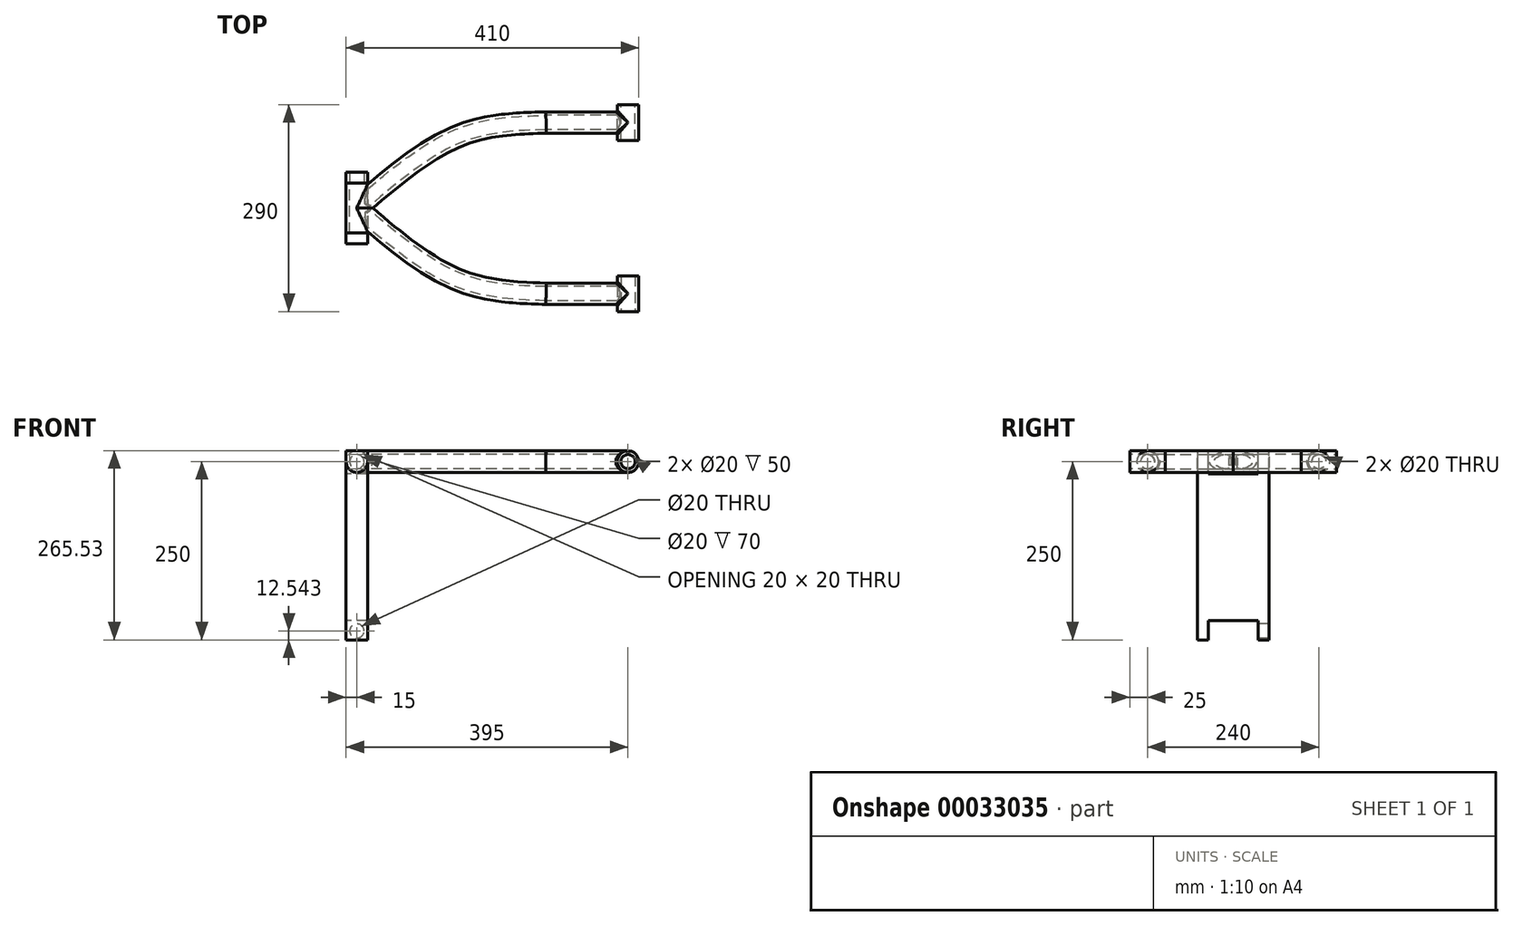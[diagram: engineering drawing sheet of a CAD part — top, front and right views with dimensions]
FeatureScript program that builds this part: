
annotation { "Feature Type Name" : "Feature", "Feature Type Description" : "" }
export const myFeature = defineFeature(function(context is Context, id is Id, definition is map)
    precondition{}
    {
        {
            var Q0;
            Q0=qCreatedBy(makeId("Front.planeOp"),FACE);
            var sketch = newSketch(context, id + "F0", { "sketchPlane" : qUnion([Q0])});
            skCircle(sketch, "E0", {"center": v(0, 0) * mm, "radius": 15 * mm});
            skCircle(sketch, "E1", {"center": v(0, 0) * mm, "radius": 10 * mm});
            skLineSegment(sketch, "E2", {"start": v(-15, 31.18) * mm, "end": v(-15, -34.32) * mm, "construction": true});
            skSolve(sketch);
        }
        {
            var Q0;
            Q0=makeQuery(id+"F0.imprint","IMPRINT",FACE,{"disambiguationData":[TD([[makeQuery(id+"F0.imprint","IMPRINT",EDGE,{"derivedFrom":sQuery(id+"F0.wireOp",EDGE,"E0")}),1.0]])]});
            extrude(context, id + "F1", {"entities" : qUnion([Q0]), "depth" : 50 * mm});
        }
        {
            var Q0;
            Q0=qCreatedBy(makeId("Right.planeOp"),FACE);
            var sketch = newSketch(context, id + "F2", { "sketchPlane" : qUnion([Q0])});
            skLineSegment(sketch, "E3", {"start": v(0, -15) * mm, "end": v(-50, -15) * mm});
            skLineSegment(sketch, "E4", {"start": v(-50, 15) * mm, "end": v(0, 15) * mm});
            skCircle(sketch, "E5", {"center": v(-25, 0) * mm, "radius": 15 * mm});
            skPoint(sketch, "E5.centerSnap0", {"position": v(-25, 15) * mm});
            skCircle(sketch, "E6", {"center": v(-25, 0) * mm, "radius": 10 * mm});
            skSolve(sketch);
        }
        {
            var Q0;
            Q0=qCreatedBy(makeId("Top.planeOp"),FACE);
            var sketch = newSketch(context, id + "F3", { "sketchPlane" : qUnion([Q0])});
            skLineSegment(sketch, "E7", {"start": v(0, -37.06) * mm, "end": v(0, -397.44) * mm, "construction": true});
            skLineSegment(sketch, "E8", {"start": v(-380, 0) * mm, "end": v(-380, -571.82) * mm, "construction": true});
            skLineSegment(sketch, "E9", {"start": v(76.72, -145) * mm, "end": v(-436.32, -145) * mm, "construction": true});
            skLineSegment(sketch, "E10", {"start": v(0, -25.32) * mm, "end": v(-114.87, -25.32) * mm});
            skFitSpline(sketch, "E11", {"points": [v(-114.87, -25.32) * mm, v(-237.42, -44.08) * mm, v(-380, -145) * mm], "startDerivative": vector(-269.22, -7.9) * mm, "endDerivative": vector(-261.26, -225.26) * mm});
            skLineSegment(sketch, "E12.MirrorCS", {"start": v(0, -264.68) * mm, "end": v(-114.87, -264.68) * mm});
            skFitSpline(sketch, "E13.MirrorCS", {"points": [v(-114.87, -264.68) * mm, v(-237.42, -245.92) * mm, v(-380, -145) * mm], "startDerivative": vector(-269.22, 7.9) * mm, "endDerivative": vector(-261.26, 225.26) * mm});
            skSolve(sketch);
        }
        {
            var Q0;
            Q0 = qSketchRegion(id + "F2", true);
            var Q1;
            Q1=sQuery(id+"F3.wireOp",EDGE,"E11");
            var Q2;
            Q2=sQuery(id+"F3.wireOp",EDGE,"E10");
            sweep(context, id + "F4", {"operationType" : NewBodyOperationType.ADD, "profiles" : qUnion([Q0]), "path" : qUnion([Q1, Q2])});
        }
        {
            var Q0;
            Q0=makeQuery(id+"F4.boolean.opBoolean","INTERSECT",EDGE,{"disambiguationData":[OD(0.0)],"derivedFrom":[makeQuery(id+"F1.opExtrude","SWEPT_FACE",FACE,{"disambiguationData":[OSD([sQuery(id+"F0.wireOp",EDGE,"E0")])]}),makeQuery(id+"F4.opSweep","SWEPT_FACE",FACE,{"disambiguationData":[OSD([sQuery(id+"F2.wireOp",EDGE,"E5"),sQuery(id+"F3.wireOp",EDGE,"ba36500d-ebc8-4f5f-b360-66259673c2d1")])]})]});
            var Q1;
            Q1=makeQuery(id+"F4.boolean.opBoolean","INTERSECT",EDGE,{"disambiguationData":[OD(1.0)],"derivedFrom":[makeQuery(id+"F1.opExtrude","SWEPT_FACE",FACE,{"disambiguationData":[OSD([sQuery(id+"F0.wireOp",EDGE,"E0")])]}),makeQuery(id+"F4.opSweep","SWEPT_FACE",FACE,{"disambiguationData":[OSD([sQuery(id+"F2.wireOp",EDGE,"E5"),sQuery(id+"F3.wireOp",EDGE,"ba36500d-ebc8-4f5f-b360-66259673c2d1")])]})]});
            fillet(context, id + "F5", {"entities" : qUnion([Q0, Q1]), "radius" : 2 * mm, "tangentPropagation" : true, "allowEdgeOverflow" : false});
        }
        {
            var Q0;
            Q0=makeQuery(id+"F1.opExtrude","CAP_FACE",FACE,{"disambiguationData":[OSD([sQuery(id+"F0.wireOp",EDGE,"E0"),sQuery(id+"F0.wireOp",EDGE,"E1")])],"isStart":false});
            var sketch = newSketch(context, id + "F6", { "sketchPlane" : qUnion([Q0])});
            skCircle(sketch, "E14", {"center": v(0, 0) * mm, "radius": 10 * mm});
            skSolve(sketch);
        }
        {
            var Q0;
            Q0 = qSketchRegion(id + "F6", true);
            var Q1;
            Q1=makeQuery(id+"F6.imprint","IMPRINT",FACE,{"disambiguationData":[TD([[makeQuery(id+"F6.imprint","IMPRINT",EDGE,{"derivedFrom":sQuery(id+"F6.wireOp",EDGE,"E14")}),1.0]])]});
            extrude(context, id + "F7", {"entities" : qUnion([Q0, Q1]), "operationType" : NewBodyOperationType.REMOVE, "endBound" : BoundingType.THROUGH_ALL, "oppositeDirection" : true, "depth" : 25 * mm});
        }
        {
            var Q0;
            Q0=qCreatedBy(makeId("Front.planeOp"),FACE);
            cPlane(context, id + "F8", {"entities" : qUnion([Q0]), "cplaneType" : CPlaneType.OFFSET, "offset" : 145 * mm, "width" : 150 * mm, "height" : 150 * mm});
        }
        {
            var Q0;
            Q0=makeQuery(id+"F1.opExtrude","SWEPT_BODY",BODY,{"disambiguationData":[OSD([sQuery(id+"F0.wireOp",EDGE,"E0"),sQuery(id+"F0.wireOp",EDGE,"E1")])]});
            var Q1;
            Q1=qCreatedBy(id+"F8.planeOp",FACE);
            mirror(context, id + "F9", {"operationType" : NewBodyOperationType.ADD, "entities" : qUnion([Q0]), "mirrorPlane" : qUnion([Q1])});
        }
        {
            var Q0;
            Q0=qCreatedBy(id+"F8.planeOp",FACE);
            var sketch = newSketch(context, id + "F10", { "sketchPlane" : qUnion([Q0])});
            skLineSegment(sketch, "E15", {"start": v(0, 0) * mm, "end": v(-405.9, 0) * mm, "construction": true});
            skCircle(sketch, "E16", {"center": v(-380, 0) * mm, "radius": 15 * mm});
            skCircle(sketch, "E17", {"center": v(-380, 0) * mm, "radius": 10 * mm});
            skPoint(sketch, "E18.0", {"position": v(-380, 15) * mm});
            skLineSegment(sketch, "E19", {"start": v(-380, 15) * mm, "end": v(-380, -15) * mm, "construction": true});
            skSolve(sketch);
        }
        {
            var Q0;
            Q0 = qSketchRegion(id + "F10", true);
            extrude(context, id + "F11", {"entities" : qUnion([Q0]), "operationType" : NewBodyOperationType.ADD, "depth" : 70 * mm, "symmetric" : true});
        }
        {
            var Q0;
            Q0=makeQuery(id+"F11.opExtrude","CAP_FACE",FACE,{"disambiguationData":[OSD([sQuery(id+"F10.wireOp",EDGE,"E16"),sQuery(id+"F10.wireOp",EDGE,"E17")])],"isStart":false});
            var sketch = newSketch(context, id + "F12", { "sketchPlane" : qUnion([Q0])});
            skCircle(sketch, "E20", {"center": v(-380, 0) * mm, "radius": 10 * mm});
            skPoint(sketch, "E20.first.point", {"position": v(-378.85, 9.93) * mm});
            skPoint(sketch, "E20.second.point", {"position": v(-373.45, -7.56) * mm});
            skPoint(sketch, "E20.third.point", {"position": v(-388.96, -4.45) * mm});
            skSolve(sketch);
        }
        {
            var Q0;
            Q0=makeQuery(id+"F12.imprint","IMPRINT",FACE,{"disambiguationData":[TD([[makeQuery(id+"F12.imprint","IMPRINT",EDGE,{"derivedFrom":sQuery(id+"F12.wireOp",EDGE,"E20")}),1.0]])]});
            extrude(context, id + "F13", {"entities" : qUnion([Q0]), "operationType" : NewBodyOperationType.REMOVE, "endBound" : BoundingType.THROUGH_ALL, "oppositeDirection" : true, "depth" : 25 * mm});
        }
        {
            var Q0;
            Q0=makeQuery(id+"F11.opExtrude","CAP_FACE",FACE,{"disambiguationData":[OSD([sQuery(id+"F10.wireOp",EDGE,"E16"),sQuery(id+"F10.wireOp",EDGE,"E17")])],"isStart":false});
            var sketch = newSketch(context, id + "F14", { "sketchPlane" : qUnion([Q0])});
            skCircle(sketch, "E21", {"center": v(-380, 0) * mm, "radius": 10 * mm});
            skSolve(sketch);
        }
        {
            var Q0;
            Q0=makeQuery(id+"F14.imprint","IMPRINT",FACE,{"disambiguationData":[TD([[makeQuery(id+"F14.imprint","IMPRINT",EDGE,{"derivedFrom":sQuery(id+"F14.wireOp",EDGE,"E21")}),1.0]])]});
            extrude(context, id + "F15", {"entities" : qUnion([Q0]), "depth" : 100 * mm});
        }
        {
            var Q0;
            Q0=makeQuery(id+"F15.opExtrude","SWEPT_BODY",BODY,{"disambiguationData":[OSD([sQuery(id+"F14.wireOp",EDGE,"E21")])]});
            var Q1;
            {var subQ0=sQuery(id+"F10.wireOp",EDGE,"E16");var subQ1=sQuery(id+"F10.wireOp",EDGE,"E17");Q1=makeQuery(id+"F11.boolean.opBoolean","SPLIT",FACE,{"disambiguationData":[TD([makeQuery(id+"F11.opExtrude","CAP_FACE",FACE,{"disambiguationData":[OSD([subQ0,subQ1])],"isStart":true})])],"derivedFrom":makeQuery(id+"F11.opExtrude","SWEPT_FACE",FACE,{"disambiguationData":[OSD([subQ0])]})});}
            transform(context, id + "F16", {"entities" : qUnion([Q0]), "transformType" : TransformType.TRANSLATION_DISTANCE, "transformDirection" : qUnion([Q1]), "distance" : 85 * mm, "makeCopy" : false});
        }
        {
            var Q0;
            Q0=makeQuery(id+"F15.opExtrude","SWEPT_FACE",FACE,{"disambiguationData":[OSD([sQuery(id+"F14.wireOp",EDGE,"E21")])]});
            cPlane(context, id + "F17", {"entities" : qUnion([Q0]), "cplaneType" : CPlaneType.LINE_ANGLE, "offset" : 150 * mm, "angle" : 90 * degree, "width" : 150 * mm, "height" : 150 * mm});
        }
        {
            var Q0;
            Q0=qCreatedBy(id+"F17.planeOp",FACE);
            var sketch = newSketch(context, id + "F18", { "sketchPlane" : qUnion([Q0])});
            skLineSegment(sketch, "E22", {"start": v(-95, 10) * mm, "end": v(-95, -10) * mm});
            skLineSegment(sketch, "E23", {"start": v(-109.96, -16.97) * mm, "end": v(-180.1, -16.97) * mm});
            skLineSegment(sketch, "E24", {"start": v(-180.1, -16.97) * mm, "end": v(-180.1, -10) * mm});
            skLineSegment(sketch, "E25", {"start": v(-195, -10) * mm, "end": v(-195, 10) * mm});
            skLineSegment(sketch, "E26", {"start": v(-95, 0) * mm, "end": v(-195, 0) * mm, "construction": true});
            skLineSegment(sketch, "E27", {"start": v(-95, -10) * mm, "end": v(-95, -120) * mm});
            skLineSegment(sketch, "E28", {"start": v(-195, -120) * mm, "end": v(-195, -10) * mm});
            skLineSegment(sketch, "E29", {"start": v(-84.47, -120) * mm, "end": v(-204.44, -120) * mm, "construction": true});
            skLineSegment(sketch, "E30", {"start": v(-180.1, -10) * mm, "end": v(-180.1, 10) * mm});
            skLineSegment(sketch, "E31", {"start": v(-95, -120) * mm, "end": v(-195, -120) * mm});
            skLineSegment(sketch, "E32.MirrorCS", {"start": v(-95, -230) * mm, "end": v(-95, -120) * mm});
            skLineSegment(sketch, "E33.MirrorCS", {"start": v(-95, -250) * mm, "end": v(-95, -230) * mm});
            skLineSegment(sketch, "E34.MirrorCS", {"start": v(-109.96, -223.03) * mm, "end": v(-180.1, -223.03) * mm});
            skLineSegment(sketch, "E35.MirrorCS", {"start": v(-195, -230) * mm, "end": v(-195, -250) * mm});
            skLineSegment(sketch, "E36.MirrorCS", {"start": v(-195, -120) * mm, "end": v(-195, -230) * mm});
            skLineSegment(sketch, "E37", {"start": v(-95, -250) * mm, "end": v(-109.96, -250) * mm});
            skLineSegment(sketch, "E38", {"start": v(-109.96, -250) * mm, "end": v(-109.96, -223.03) * mm});
            skLineSegment(sketch, "E39", {"start": v(-180.1, -250) * mm, "end": v(-195, -250) * mm});
            skLineSegment(sketch, "E40", {"start": v(-109.96, -16.97) * mm, "end": v(-109.96, 10) * mm});
            skLineSegment(sketch, "E41", {"start": v(-95, 10) * mm, "end": v(-95, 15.53) * mm});
            skLineSegment(sketch, "E42", {"start": v(-95, 15.53) * mm, "end": v(-109.96, 15.53) * mm});
            skLineSegment(sketch, "E43", {"start": v(-180.1, 10) * mm, "end": v(-180.1, 15.47) * mm});
            skLineSegment(sketch, "E44", {"start": v(-180.1, 15.47) * mm, "end": v(-195, 15.47) * mm});
            skLineSegment(sketch, "E45", {"start": v(-195, 15.47) * mm, "end": v(-195, 10) * mm});
            skLineSegment(sketch, "E46", {"start": v(-109.96, 10) * mm, "end": v(-109.96, 15.53) * mm});
            skLineSegment(sketch, "E47", {"start": v(-180.1, -250) * mm, "end": v(-180.1, -223.03) * mm});
            skSolve(sketch);
        }
        {
            var Q0;
            Q0=makeQuery(id+"F18.imprint","IMPRINT",FACE,{"disambiguationData":[TD([[makeQuery(id+"F18.imprint","IMPRINT",EDGE,{"derivedFrom":sQuery(id+"F18.wireOp",EDGE,"E31")}),1.0]])]});
            var Q1;
            {var subQ2=sQuery(id+"F18.wireOp",EDGE,"E22");Q1=makeQuery(id+"F18.imprint","IMPRINT",FACE,{"disambiguationData":[TD([[makeQuery(id+"F18.imprint","IMPRINT",EDGE,{"derivedFrom":subQ2}),-1.0]])]});}
            extrude(context, id + "F19", {"entities" : qUnion([Q0, Q1]), "operationType" : NewBodyOperationType.ADD, "depth" : 30 * mm, "symmetric" : true});
        }
        {
            var Q0;
            Q0=makeQuery(id+"F19.opExtrude","SWEPT_FACE",FACE,{"disambiguationData":[OSD([sQuery(id+"F18.wireOp",EDGE,"E38")])]});
            var sketch = newSketch(context, id + "F20", { "sketchPlane" : qUnion([Q0])});
            skCircle(sketch, "E48", {"center": v(-380, -237.46) * mm, "radius": 10 * mm});
            skLineSegment(sketch, "E49", {"start": v(-380, -250) * mm, "end": v(-380, -224.91) * mm, "construction": true});
            skSolve(sketch);
        }
        {
            var Q0;
            Q0=makeQuery(id+"F20.imprint","IMPRINT",FACE,{"disambiguationData":[TD([[makeQuery(id+"F20.imprint","IMPRINT",EDGE,{"derivedFrom":sQuery(id+"F20.wireOp",EDGE,"E48")}),1.0]])]});
            extrude(context, id + "F21", {"entities" : qUnion([Q0]), "operationType" : NewBodyOperationType.REMOVE, "endBound" : BoundingType.THROUGH_ALL, "oppositeDirection" : true, "depth" : 25 * mm});
        }
    });
